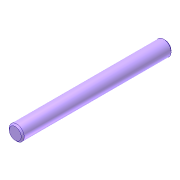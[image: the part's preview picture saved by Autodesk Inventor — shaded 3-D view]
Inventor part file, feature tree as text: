
AUTODESK INVENTOR PART (.ipt)
format: ipt  version: unknown  size: 165,376 bytes
history: native  units: in
note: dims shown in document units (in); Inventor stores cm internally (conversion verified against a paired STEP export)
features: extrude x1, chamfer x1, sketch x1
ambient origin geometry x8: Origin, YZ Plane, XZ Plane, XY Plane, X Axis, Y Axis, Z Axis, Center Point
feature tree (3):
  extrude  "Extrusion42"  Depth=0.0394in
  chamfer  "Chamfer6"  Distance=0.3937in
  sketch  "Sketch47"  dims[d21=0.7874in d264=0.0394in d265=0.3937in d266=0.0in d267=0.0039in d268=0.0787in d269=45.0deg]
